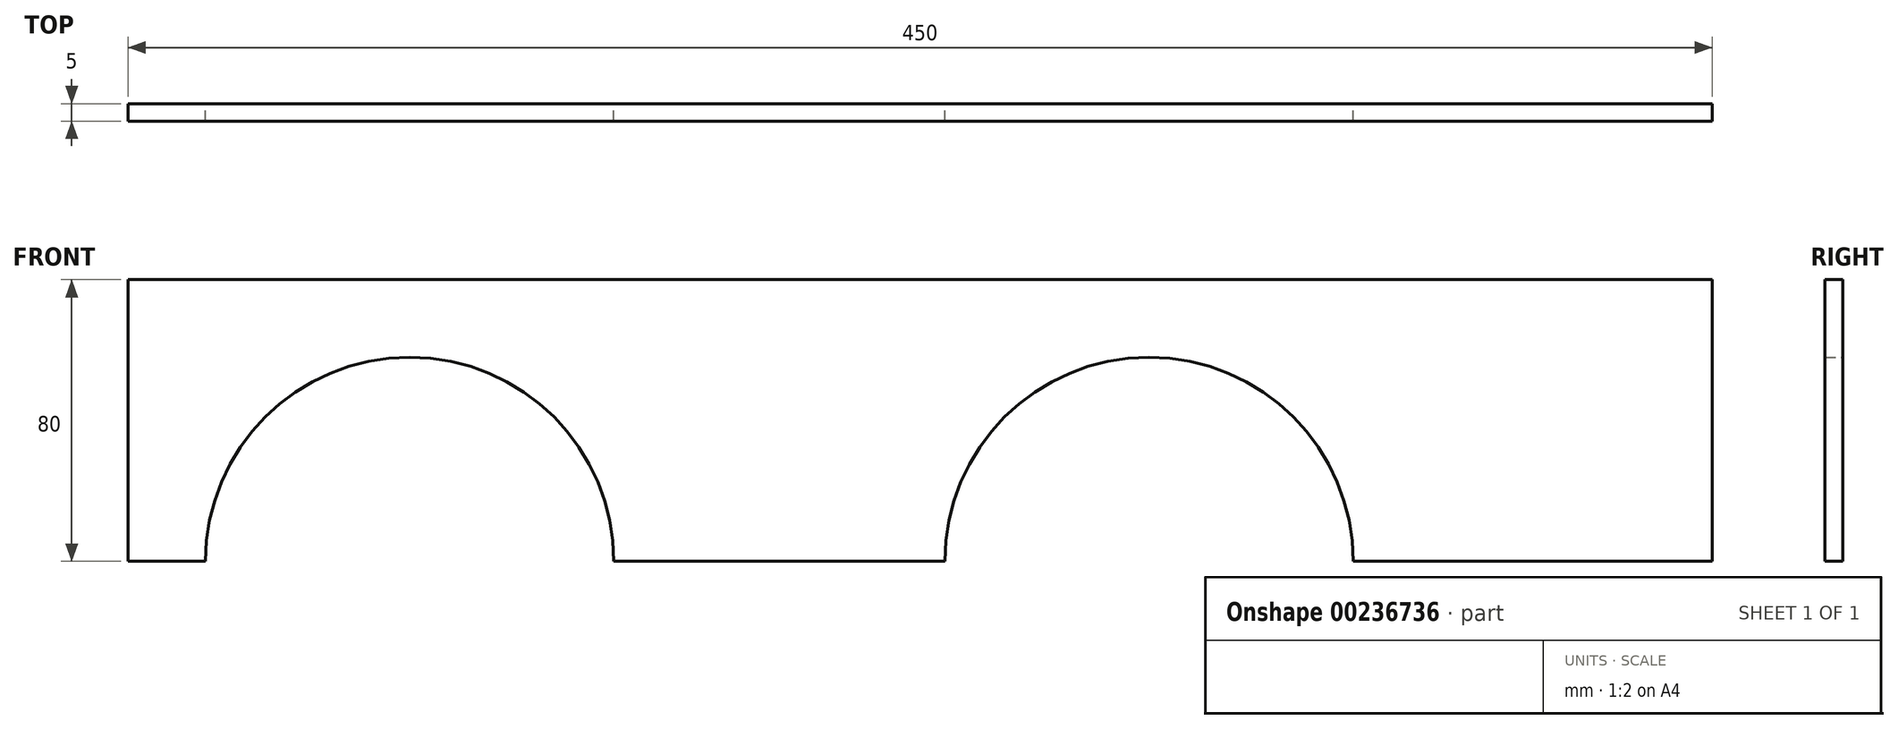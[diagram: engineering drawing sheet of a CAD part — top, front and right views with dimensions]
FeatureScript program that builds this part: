
annotation { "Feature Type Name" : "Feature", "Feature Type Description" : "" }
export const myFeature = defineFeature(function(context is Context, id is Id, definition is map)
    precondition{}
    {
        {
            var Q0;
            Q0=qCreatedBy(makeId("Front.planeOp"),FACE);
            var sketch = newSketch(context, id + "F0", { "sketchPlane" : qUnion([Q0])});
            skLineSegment(sketch, "E0.bottom", {"start": v(0, 0) * mm, "end": v(22, 0) * mm});
            skLineSegment(sketch, "E0.top", {"start": v(0, 80) * mm, "end": v(450, 80) * mm});
            skLineSegment(sketch, "E0.left", {"start": v(0, 0) * mm, "end": v(0, 80) * mm});
            skLineSegment(sketch, "E0.right", {"start": v(450, 0) * mm, "end": v(450, 80) * mm});
            skArc(sketch, "E1", {"start": v(138, 0) * mm, "mid": v(80, 58) * mm, "end": v(22, 0) * mm});
            skArc(sketch, "E2", {"start": v(348, 0) * mm, "mid": v(290, 58) * mm, "end": v(232, 0) * mm});
            skLineSegment(sketch, "E3.trimOffspring", {"start": v(348, 0) * mm, "end": v(450, 0) * mm});
            skLineSegment(sketch, "E4", {"start": v(138, 0) * mm, "end": v(232, 0) * mm});
            skSolve(sketch);
        }
        {
            var Q0;
            Q0 = qSketchRegion(id + "F0", true);
            extrude(context, id + "F1", {"entities" : qUnion([Q0]), "depth" : 5 * mm, "offsetDistance" : 25 * mm});
        }
    });
